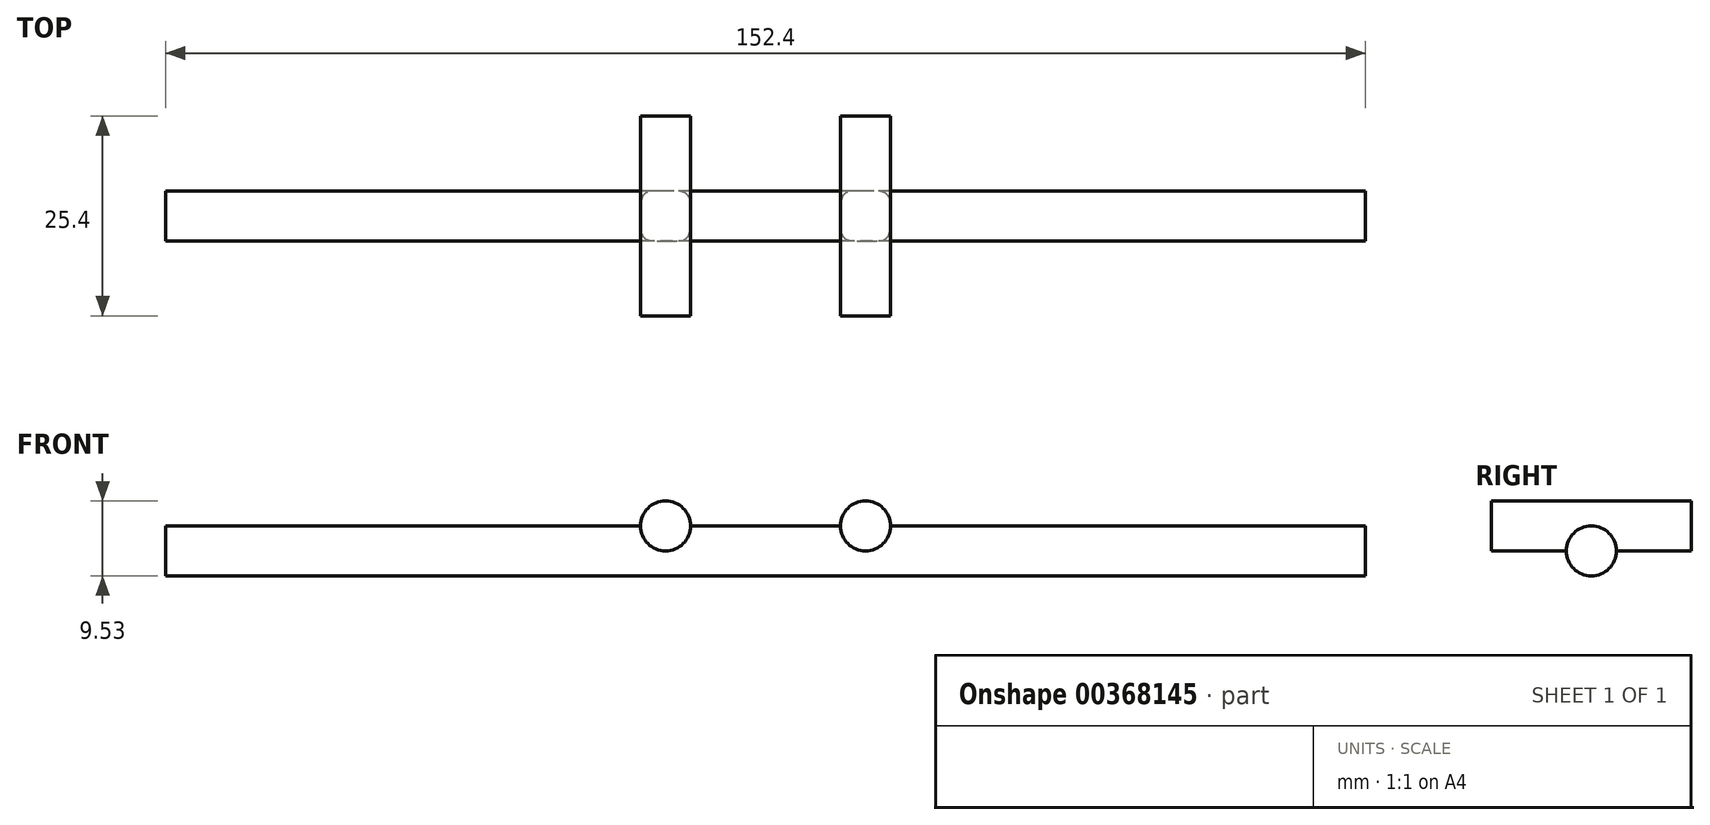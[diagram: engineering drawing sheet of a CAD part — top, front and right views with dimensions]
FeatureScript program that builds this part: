
annotation { "Feature Type Name" : "Feature", "Feature Type Description" : "" }
export const myFeature = defineFeature(function(context is Context, id is Id, definition is map)
    precondition{}
    {
        {
            var Q0;
            Q0=qCreatedBy(makeId("Right.planeOp"),FACE);
            var sketch = newSketch(context, id + "F0", { "sketchPlane" : qUnion([Q0])});
            skCircle(sketch, "E0", {"center": v(0, -3.18) * mm, "radius": 3.18 * mm});
            skSolve(sketch);
        }
        {
            var Q0;
            Q0 = qSketchRegion(id + "F0", true);
            var Q1;
            Q1 = qSketchRegion(id + "F2", true);
            extrude(context, id + "F1", {"entities" : qUnion([Q0, Q1]), "depth" : 152.4 * mm, "offsetDistance" : 25.4 * mm});
        }
        {
            var Q0;
            Q0=qCreatedBy(makeId("Front.planeOp"),FACE);
            var sketch = newSketch(context, id + "F2", { "sketchPlane" : qUnion([Q0])});
            skLineSegment(sketch, "E1", {"start": v(76.2, 0) * mm, "end": v(88.9, 0) * mm});
            skCircle(sketch, "E2", {"center": v(88.9, 0) * mm, "radius": 3.18 * mm});
            skLineSegment(sketch, "E3", {"start": v(76.2, 0) * mm, "end": v(63.5, 0) * mm});
            skCircle(sketch, "E4", {"center": v(63.5, 0) * mm, "radius": 3.18 * mm});
            skSolve(sketch);
        }
        {
            var Q0;
            Q0 = qSketchRegion(id + "F2", true);
            extrude(context, id + "F3", {"entities" : qUnion([Q0]), "operationType" : NewBodyOperationType.ADD, "depth" : 25.4 * mm, "offsetDistance" : 25.4 * mm, "symmetric" : true});
        }
    });
